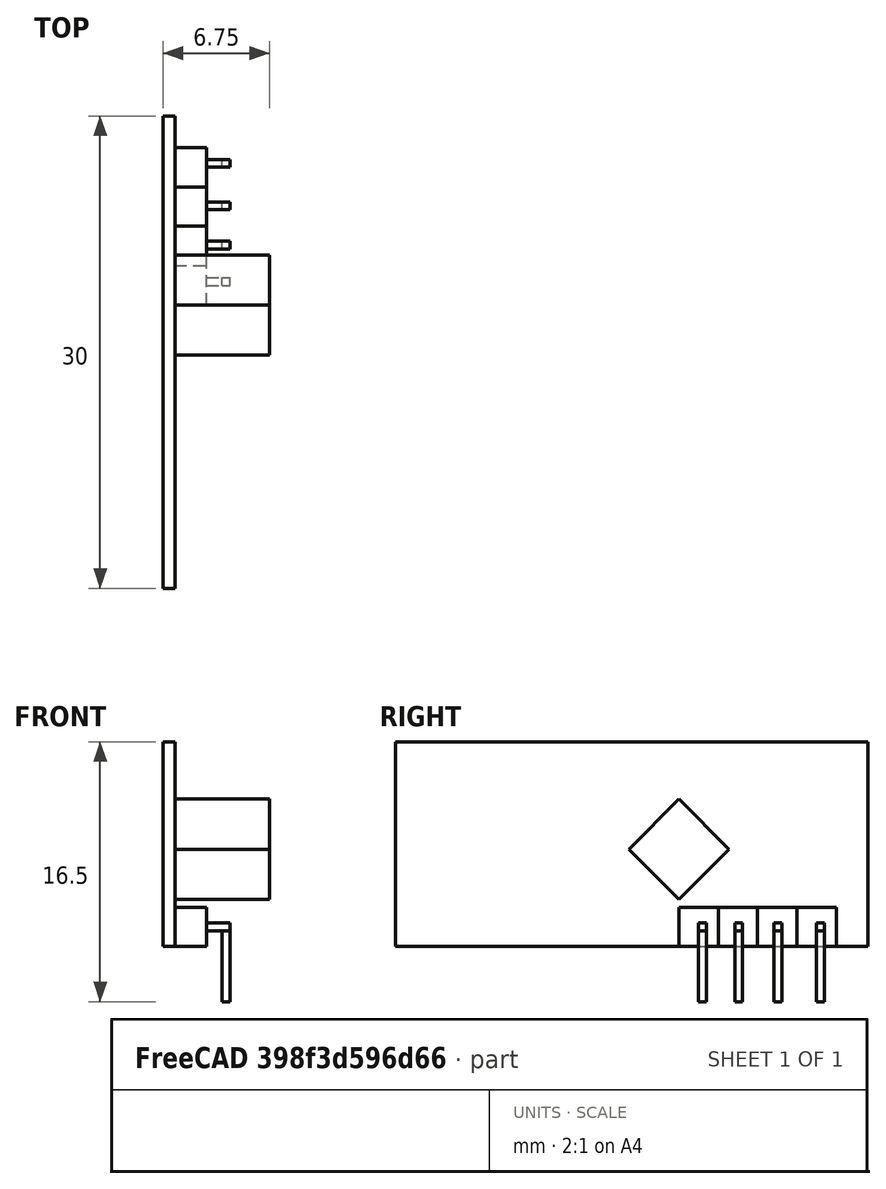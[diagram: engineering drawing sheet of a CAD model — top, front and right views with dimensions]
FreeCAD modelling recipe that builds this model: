
FCSTD DOCUMENT  (FreeCAD 0.16R)
Label: 433_MHz_Receiver
License: All rights reserved
LicenseURL: http://en.wikipedia.org/wiki/All_rights_reserved
objects: Part::Box×14, Part::Helix×1
note: 15 computed .brp shape members not serialized (recipe doc carries the construction recipe); baked Part::Feature solids carry a one-line shape summary decoded from their .brp

FEATURE [Part::Box] Box  label="Cube"
  Height = 13
  Length = 0.75
  Placement = pos=(0.25,-12,0) rot=(0,0,1;0rad)
  Width = 30
FEATURE [Part::Box] Box001  label="Cube001"
  Height = 2.5
  Length = 2
  Placement = pos=(1,6,0) rot=(0,0,1;0rad)
  Width = 2.5
FEATURE [Part::Box] Box002  label="Cube002"
  Height = 2.5
  Length = 2
  Placement = pos=(1,8.5,0) rot=(0,0,1;0rad)
  Width = 2.5
FEATURE [Part::Box] Box003  label="Cube003"
  Height = 2.5
  Length = 2
  Placement = pos=(1,11,0) rot=(0,0,1;0rad)
  Width = 2.5
FEATURE [Part::Box] Box004  label="Cube004"
  Height = 0.5
  Length = 1.5
  Placement = pos=(3,7.25,1) rot=(0,0,1;0rad)
  Width = 0.5
FEATURE [Part::Box] Box005  label="Cube005"
  Height = 4.5
  Length = 0.5
  Placement = pos=(4,7.25,-3.5) rot=(0,0,1;0rad)
  Width = 0.5
FEATURE [Part::Helix] Helix001  label="Hélice"
  Angle = 0
  Height = 2
  LocalCoord = 0
  Pitch = 0.6
  Placement = pos=(3.2,-7,0.5) rot=(1,0,0;0.366519rad)
  Radius = 2
  Style = 1
FEATURE [Part::Box] Box006  label="Cube006"
  Height = 0.5
  Length = 1.5
  Placement = pos=(3,9.55,1) rot=(0,0,1;0rad)
  Width = 0.5
FEATURE [Part::Box] Box007  label="Cube007"
  Height = 4.5
  Length = 0.5
  Placement = pos=(4,9.55,-3.5) rot=(0,0,1;0rad)
  Width = 0.5
FEATURE [Part::Box] Box008  label="Cube008"
  Height = 0.5
  Length = 1.5
  Placement = pos=(3,12.05,1) rot=(0,0,1;0rad)
  Width = 0.5
FEATURE [Part::Box] Box009  label="Cube009"
  Height = 4.5
  Length = 0.5
  Placement = pos=(4,12.05,-3.5) rot=(0,0,1;0rad)
  Width = 0.5
FEATURE [Part::Box] Box010  label="Cube010"
  Height = 2.5
  Length = 2
  Placement = pos=(1,13.5,0) rot=(0,0,1;0rad)
  Width = 2.5
FEATURE [Part::Box] Box011  label="Cube011"
  Height = 0.5
  Length = 1.5
  Placement = pos=(3,14.75,1) rot=(0,0,1;0rad)
  Width = 0.5
FEATURE [Part::Box] Box012  label="Cube012"
  Height = 4.5
  Length = 0.5
  Placement = pos=(4,14.75,-3.5) rot=(0,0,1;0rad)
  Width = 0.5
FEATURE [Part::Box] Box013  label="Cube013"
  Height = 4.5
  Length = 6
  Placement = pos=(1,6,3) rot=(1,0,0;0.785398rad)
  Width = 4.5
